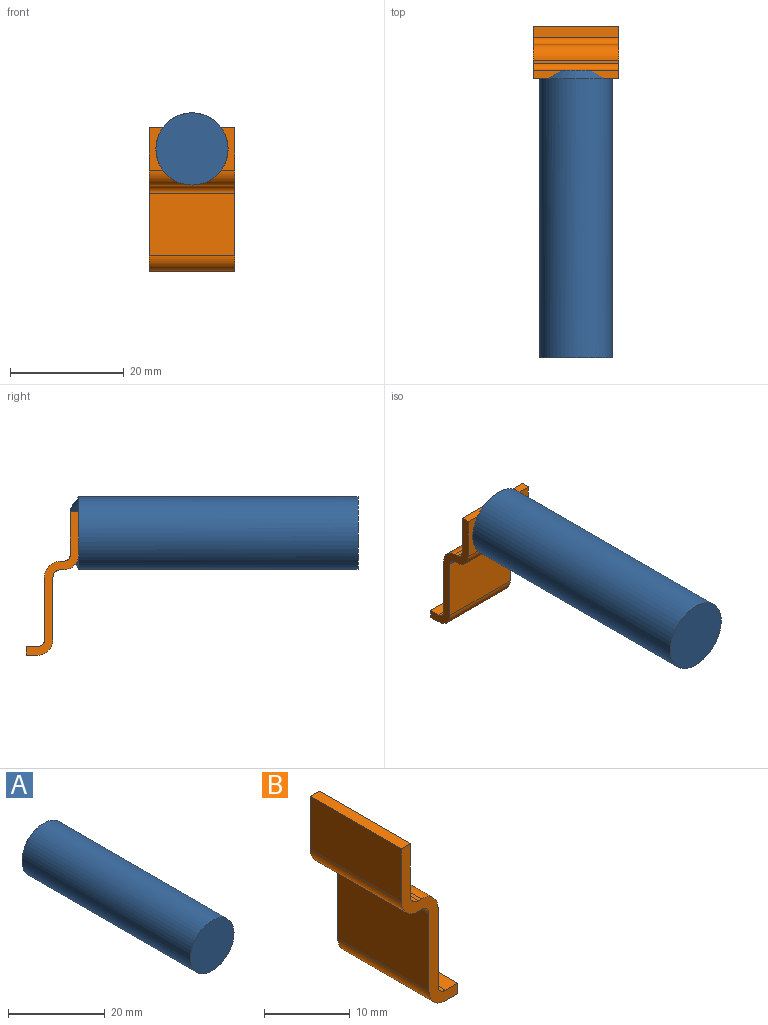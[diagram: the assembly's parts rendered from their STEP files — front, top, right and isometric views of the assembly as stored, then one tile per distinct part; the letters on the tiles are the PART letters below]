
ASSEMBLY  parts=2 mates=1
PART A: 4 faces, bbox 12.7x50.6x12.7 mm
  f0: cylinder r=6.35mm len=49.14mm, axis (0,-1,0), area 1960.4mm2, adj f2,f3
  f1: plane 8.7x8.7mm, normal (0,1,0), area 59.4mm2, adj f3
  f2: plane 12.7x12.7mm, normal (0,-1,0), area 126.7mm2, adj f0
  f3: cone r=6.35mm half-angle=53.1deg, axis (0,-1,0), area 84mm2, adj f0,f1
PART B: 18 faces, bbox 9.3x15x25.3 mm
  f0: plane 15x1.5mm, normal (0,0,1), area 22.5mm2, adj f1,f3,f7,f14
  f1: plane 25.28x9.3mm, normal (0,1,0), area 45.7mm2, adj f0,f2,f4,f5,f6,f7,f8,f9
  f2: plane 15x1.5mm, normal (1,0,0), area 22.5mm2, adj f1,f3,f5,f12
  f3: plane 25.28x9.3mm, normal (0,-1,0), area 45.7mm2, adj f0,f2,f4,f5,f6,f7,f8,f9
  f4: plane 15x11mm, normal (-1,0,0), area 165mm2, adj f1,f3,f8,f9
  f5: plane 15x2mm, normal (0,0,-1), area 30mm2, adj f1,f2,f3,f9
  f6: plane 15x0.55mm, normal (0,0,-1), area 8.3mm2, adj f1,f3,f8,f10
  f7: plane 15x7.53mm, normal (-1,0,0), area 112.9mm2, adj f0,f1,f3,f10
  f8: cylinder r=1.25mm len=15mm, axis (0,1,0), area 29.5mm2, adj f1,f3,f4,f6
  f9: cylinder r=2.75mm len=15mm, axis (0,-1,0), area 64.8mm2, adj f1,f3,f4,f5
  f10: cylinder r=2.75mm len=15mm, axis (0,-1,0), area 64.8mm2, adj f1,f3,f6,f7
  f11: plane 15x11mm, normal (1,0,0), area 165mm2, adj f1,f3,f15,f16
  f12: plane 15x2mm, normal (0,0,1), area 30mm2, adj f1,f2,f3,f16
  f13: plane 15x0.55mm, normal (0,0,1), area 8.3mm2, adj f1,f3,f15,f17
  f14: plane 15x7.53mm, normal (1,0,0), area 112.9mm2, adj f0,f1,f3,f17
  f15: cylinder r=2.75mm len=15mm, axis (0,1,0), area 64.8mm2, adj f1,f3,f11,f13
  f16: cylinder r=1.25mm len=15mm, axis (0,-1,0), area 29.5mm2, adj f1,f3,f11,f12
  f17: cylinder r=1.25mm len=15mm, axis (0,-1,0), area 29.5mm2, adj f1,f3,f13,f14
PLACE A t=(4.65,-4.88,13.46)mm
PLACE B rot(axis=(0,0,1),90deg) t=(4.65,-4.13,5.22)mm
MATE parallel B.f7 <-> A.f0  axis (0,-1,0) through (4.65,-13.43,3.36)mm
